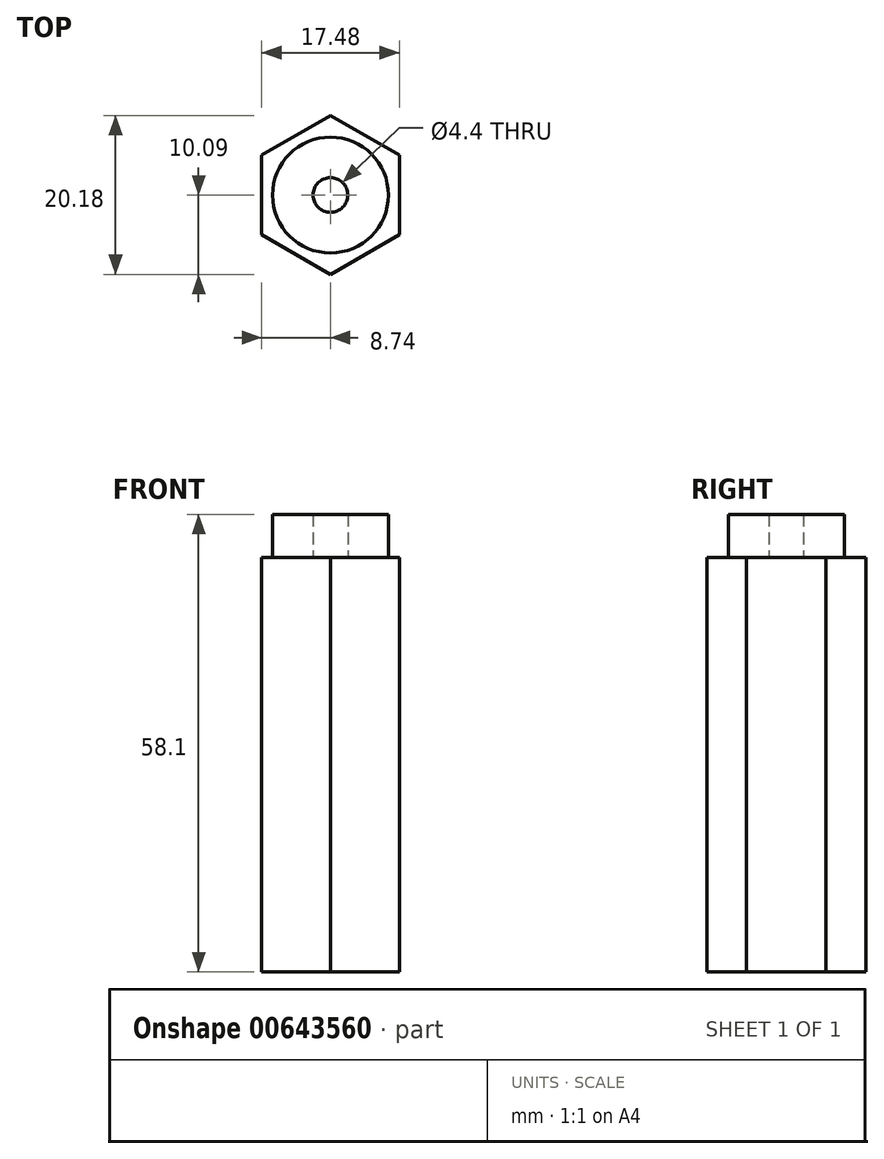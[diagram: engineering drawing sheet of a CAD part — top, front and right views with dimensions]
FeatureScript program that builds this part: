
annotation { "Feature Type Name" : "Feature", "Feature Type Description" : "" }
export const myFeature = defineFeature(function(context is Context, id is Id, definition is map)
    precondition{}
    {
        {
            var Q0;
            Q0=qCreatedBy(makeId("Top.planeOp"),FACE);
            var sketch = newSketch(context, id + "F0", { "sketchPlane" : qUnion([Q0])});
            skCircle(sketch, "E0.cCircle", {"center": v(0, 0) * mm, "radius": 8.74 * mm, "construction": true});
            skLineSegment(sketch, "E0.0", {"start": v(8.74, 5.05) * mm, "end": v(8.74, -5.05) * mm});
            skLineSegment(sketch, "E0.1", {"start": v(8.74, -5.05) * mm, "end": v(0, -10.1) * mm});
            skLineSegment(sketch, "E0.2", {"start": v(0, -10.1) * mm, "end": v(-8.74, -5.05) * mm});
            skLineSegment(sketch, "E0.3", {"start": v(-8.74, -5.05) * mm, "end": v(-8.74, 5.05) * mm});
            skLineSegment(sketch, "E0.4", {"start": v(-8.74, 5.05) * mm, "end": v(0, 10.1) * mm});
            skLineSegment(sketch, "E0.5", {"start": v(0, 10.1) * mm, "end": v(8.74, 5.05) * mm});
            skPoint(sketch, "E0.0.midPoint", {"position": v(8.74, 0) * mm});
            skSolve(sketch);
        }
        {
            var Q0;
            Q0=makeQuery(id+"F0.imprint","IMPRINT",FACE,{"disambiguationData":[TD([[makeQuery(id+"F0.imprint","IMPRINT",EDGE,{"derivedFrom":sQuery(id+"F0.wireOp",EDGE,"E0.0")}),-1.0]])]});
            extrude(context, id + "F1", {"entities" : qUnion([Q0]), "oppositeDirection" : true, "depth" : 52.64 * mm, "offsetDistance" : 25 * mm});
        }
        {
            var Q0;
            Q0=qCreatedBy(makeId("Top.planeOp"),FACE);
            var sketch = newSketch(context, id + "F2", { "sketchPlane" : qUnion([Q0])});
            skCircle(sketch, "E1", {"center": v(0, 0) * mm, "radius": 7.36 * mm});
            skSolve(sketch);
        }
        {
            var Q0;
            Q0=makeQuery(id+"F2.imprint","IMPRINT",FACE,{"disambiguationData":[TD([[makeQuery(id+"F2.imprint","IMPRINT",EDGE,{"derivedFrom":sQuery(id+"F2.wireOp",EDGE,"E1")}),1.0]])]});
            var Q1;
            Q1=sQuery(id+"F2.wireOp",EDGE,"E1");
            extrude(context, id + "F3", {"entities" : qUnion([Q0]), "surfaceEntities" : qUnion([Q1]), "depth" : 5.46 * mm, "offsetDistance" : 25 * mm});
        }
        {
            var Q0;
            Q0=qCreatedBy(makeId("Top.planeOp"),FACE);
            var sketch = newSketch(context, id + "F4", { "sketchPlane" : qUnion([Q0])});
            skCircle(sketch, "E2", {"center": v(0, 0) * mm, "radius": 2.2 * mm});
            skSolve(sketch);
        }
        {
            var Q0;
            Q0=sQuery(id+"F4.wireOp",VERTEX,"E2.center");
            var Q1;
            Q1=makeQuery(id+"F3.opExtrude","SWEPT_BODY",BODY,{"disambiguationData":[OSD([sQuery(id+"F2.wireOp",EDGE,"E1")])]});
            hole(context, id + "F5", {"style" : HoleStyle.SIMPLE, "endStyle" : HoleEndStyle.THROUGH, "oppositeDirection" : true, "holeDiameter" : 4.4 * mm, "majorDiameter" : 5 * mm, "isTappedThrough" : true, "tappedDepth" : 12 * mm, "tapClearance" : 3, "locations" : qUnion([Q0]), "scope" : qUnion([Q1])});
        }
    });
